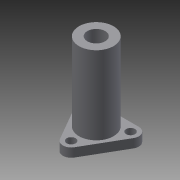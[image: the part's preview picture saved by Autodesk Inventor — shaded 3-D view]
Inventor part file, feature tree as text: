
AUTODESK INVENTOR PART (.ipt)
format: ipt  version: 2013 (Build 170138000, 138)  size: 108,544 bytes
history: native  units: in
note: dims shown in document units (in); Inventor stores cm internally (conversion verified against a paired STEP export)
features: extrude x3, sketch x3
ambient origin geometry x8: Origin, YZ Plane, XZ Plane, XY Plane, X Axis, Y Axis, Z Axis, Center Point
bodies: Solid1 (feature_tree)
feature tree (6):
  extrude  "Extrusion1"  Depth=0.4in
  extrude  "Extrusion2"  Depth=1.4in
  extrude  "Extrusion3"  Depth=0.185in
  sketch  "Sketch1"  dims[d0=0.775in d1=0.4in]
  sketch  "Sketch2"  dims[d2=1.75in d3=0.0in d4=1.4in]
  sketch  "Sketch3"  dims[d5=1.4in d6=0.185in d7=0.185in d8=0.185in d9=0.2in d10=0.0in d11=0.2in d12=0.2in d13=0.2in d14=0.2in d15=0.0in]
